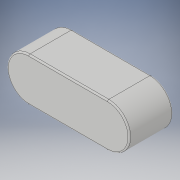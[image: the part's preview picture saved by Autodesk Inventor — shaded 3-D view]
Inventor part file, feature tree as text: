
AUTODESK INVENTOR PART (.ipt)
format: ipt  version: 2019.4 (Build 234330000, 330)  size: 116,736 bytes
history: native  units: mm
features: other x1, extrude x1, fillet x1, sketch x1
ambient origin geometry x8: Origin, YZ Plane, XZ Plane, XY Plane, X Axis, Y Axis, Z Axis, Center Point
bodies: Body1 (feature_tree)
feature tree (4):
  other  "實體1"
  extrude  "擠出1"  Depth=9.0mm
  fillet  "圓角1"  Radius=5.0mm
  sketch  "草圖1"
